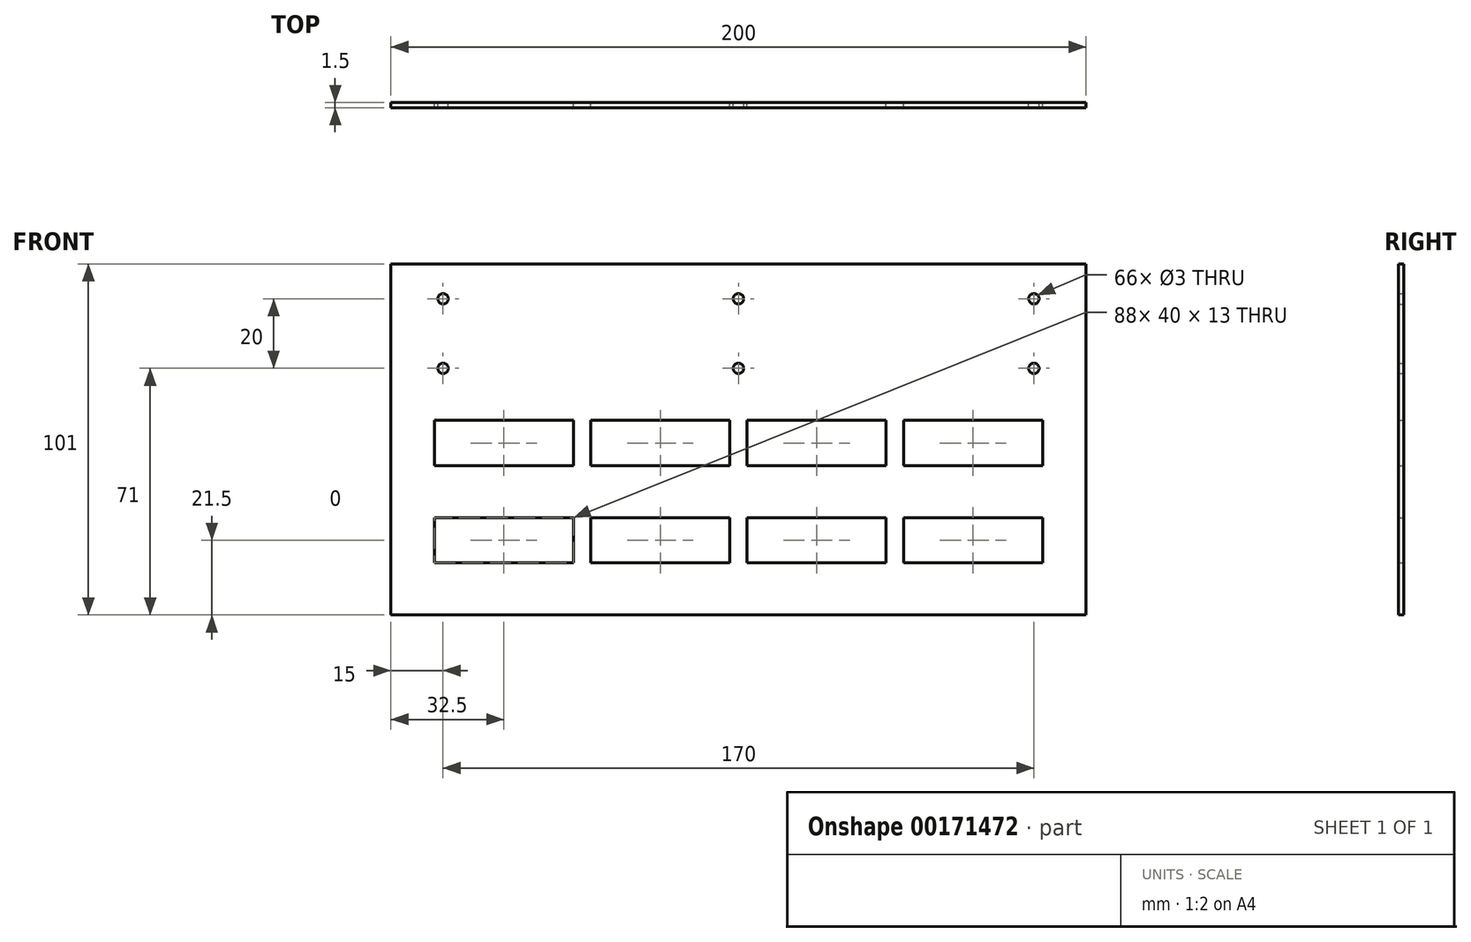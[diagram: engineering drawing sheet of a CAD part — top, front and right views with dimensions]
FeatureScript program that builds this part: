
annotation { "Feature Type Name" : "Feature", "Feature Type Description" : "" }
export const myFeature = defineFeature(function(context is Context, id is Id, definition is map)
    precondition{}
    {
        {
            var Q0;
            Q0=qCreatedBy(makeId("Front.planeOp"),FACE);
            var sketch = newSketch(context, id + "F0", { "sketchPlane" : qUnion([Q0])});
            skLineSegment(sketch, "E0.bottom", {"start": v(0, 0) * mm, "end": v(200, 0) * mm});
            skLineSegment(sketch, "E0.top", {"start": v(0, 101) * mm, "end": v(200, 101) * mm});
            skLineSegment(sketch, "E0.left", {"start": v(0, 0) * mm, "end": v(0, 101) * mm});
            skLineSegment(sketch, "E0.right", {"start": v(200, 0) * mm, "end": v(200, 101) * mm});
            skPoint(sketch, "E1", {"position": v(12.5, 15) * mm});
            skLineSegment(sketch, "E2.bottom", {"start": v(12.5, 15) * mm, "end": v(52.5, 15) * mm});
            skLineSegment(sketch, "E2.top", {"start": v(12.5, 28) * mm, "end": v(52.5, 28) * mm});
            skLineSegment(sketch, "E2.left", {"start": v(12.5, 15) * mm, "end": v(12.5, 28) * mm});
            skLineSegment(sketch, "E2.right", {"start": v(52.5, 15) * mm, "end": v(52.5, 28) * mm});
            skPoint(sketch, "E3", {"position": v(57.5, 15) * mm});
            skLineSegment(sketch, "E4.bottom", {"start": v(57.5, 15) * mm, "end": v(97.5, 15) * mm});
            skLineSegment(sketch, "E4.top", {"start": v(57.5, 28) * mm, "end": v(97.5, 28) * mm});
            skLineSegment(sketch, "E4.left", {"start": v(57.5, 15) * mm, "end": v(57.5, 28) * mm});
            skLineSegment(sketch, "E4.right", {"start": v(97.5, 15) * mm, "end": v(97.5, 28) * mm});
            skPoint(sketch, "E5", {"position": v(102.5, 15) * mm});
            skLineSegment(sketch, "E6.bottom", {"start": v(102.5, 15) * mm, "end": v(142.5, 15) * mm});
            skLineSegment(sketch, "E6.top", {"start": v(102.5, 28) * mm, "end": v(142.5, 28) * mm});
            skLineSegment(sketch, "E6.left", {"start": v(102.5, 15) * mm, "end": v(102.5, 28) * mm});
            skLineSegment(sketch, "E6.right", {"start": v(142.5, 15) * mm, "end": v(142.5, 28) * mm});
            skPoint(sketch, "E7", {"position": v(147.5, 15) * mm});
            skLineSegment(sketch, "E8.bottom", {"start": v(147.5, 15) * mm, "end": v(187.5, 15) * mm});
            skLineSegment(sketch, "E8.top", {"start": v(147.5, 28) * mm, "end": v(187.5, 28) * mm});
            skLineSegment(sketch, "E8.left", {"start": v(147.5, 15) * mm, "end": v(147.5, 28) * mm});
            skLineSegment(sketch, "E8.right", {"start": v(187.5, 15) * mm, "end": v(187.5, 28) * mm});
            skPoint(sketch, "E9", {"position": v(12.5, 35.5) * mm});
            skLineSegment(sketch, "E10", {"start": v(12.5, 35.5) * mm, "end": v(187.5, 35.5) * mm, "construction": true});
            skLineSegment(sketch, "E11.MirrorCS", {"start": v(12.5, 43) * mm, "end": v(52.5, 43) * mm});
            skLineSegment(sketch, "E12.MirrorCS", {"start": v(12.5, 56) * mm, "end": v(12.5, 43) * mm});
            skLineSegment(sketch, "E13.MirrorCS", {"start": v(12.5, 56) * mm, "end": v(52.5, 56) * mm});
            skLineSegment(sketch, "E14.MirrorCS", {"start": v(52.5, 56) * mm, "end": v(52.5, 43) * mm});
            skLineSegment(sketch, "E15.MirrorCS", {"start": v(57.5, 56) * mm, "end": v(57.5, 43) * mm});
            skLineSegment(sketch, "E16.MirrorCS", {"start": v(57.5, 43) * mm, "end": v(97.5, 43) * mm});
            skLineSegment(sketch, "E17.MirrorCS", {"start": v(57.5, 56) * mm, "end": v(97.5, 56) * mm});
            skLineSegment(sketch, "E18.MirrorCS", {"start": v(97.5, 56) * mm, "end": v(97.5, 43) * mm});
            skLineSegment(sketch, "E19.MirrorCS", {"start": v(102.5, 56) * mm, "end": v(102.5, 43) * mm});
            skLineSegment(sketch, "E20.MirrorCS", {"start": v(102.5, 43) * mm, "end": v(142.5, 43) * mm});
            skLineSegment(sketch, "E21.MirrorCS", {"start": v(102.5, 56) * mm, "end": v(142.5, 56) * mm});
            skLineSegment(sketch, "E22.MirrorCS", {"start": v(142.5, 56) * mm, "end": v(142.5, 43) * mm});
            skLineSegment(sketch, "E23.MirrorCS", {"start": v(147.5, 56) * mm, "end": v(147.5, 43) * mm});
            skLineSegment(sketch, "E24.MirrorCS", {"start": v(147.5, 56) * mm, "end": v(187.5, 56) * mm});
            skLineSegment(sketch, "E25.MirrorCS", {"start": v(187.5, 56) * mm, "end": v(187.5, 43) * mm});
            skLineSegment(sketch, "E26.MirrorCS", {"start": v(147.5, 43) * mm, "end": v(187.5, 43) * mm});
            skPoint(sketch, "E27", {"position": v(0, 61) * mm});
            skLineSegment(sketch, "E28", {"start": v(0, 61) * mm, "end": v(200, 61) * mm});
            skPoint(sketch, "E29", {"position": v(100, 91) * mm});
            skPoint(sketch, "E30", {"position": v(100, 71) * mm});
            skPoint(sketch, "E31", {"position": v(200, 61) * mm});
            skCircle(sketch, "E32", {"center": v(100, 91) * mm, "radius": 1.5 * mm});
            skCircle(sketch, "E33", {"center": v(100, 71) * mm, "radius": 1.5 * mm});
            skPoint(sketch, "E34", {"position": v(185, 91) * mm});
            skPoint(sketch, "E35", {"position": v(185, 71) * mm});
            skPoint(sketch, "E36", {"position": v(15, 91) * mm});
            skPoint(sketch, "E37", {"position": v(15, 71) * mm});
            skCircle(sketch, "E38", {"center": v(15, 91) * mm, "radius": 1.5 * mm});
            skCircle(sketch, "E39", {"center": v(15, 71) * mm, "radius": 1.5 * mm});
            skCircle(sketch, "E40", {"center": v(185, 91) * mm, "radius": 1.5 * mm});
            skCircle(sketch, "E41", {"center": v(185, 71) * mm, "radius": 1.5 * mm});
            skSolve(sketch);
        }
        {
            var Q0;
            Q0 = qSketchRegion(id + "F0", true);
            extrude(context, id + "F1", {"entities" : qUnion([Q0]), "depth" : 1.5 * mm});
        }
    });
